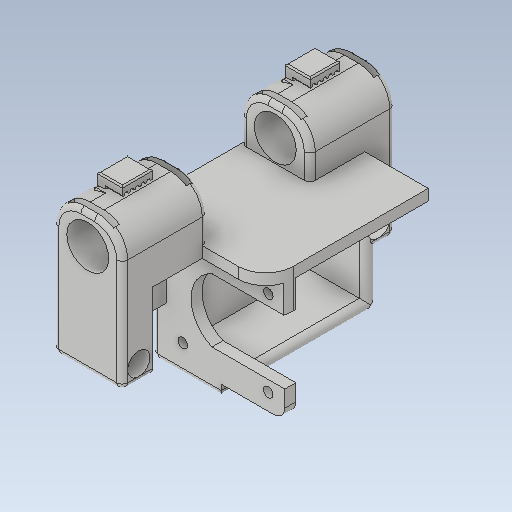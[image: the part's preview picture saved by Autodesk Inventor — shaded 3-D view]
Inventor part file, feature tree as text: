
AUTODESK INVENTOR PART (.ipt)
format: ipt  version: 2020 (Build 240168000, 168)  size: 683,008 bytes
history: native  units: in
note: dims shown in document units (in); Inventor stores cm internally (conversion verified against a paired STEP export)
features: projected_geometry x27, extrude x16, sketch x16, fillet x8, plane x1, pattern_linear x1, mirror x1
ambient origin geometry x8: Origin, YZ Plane, XZ Plane, XY Plane, X Axis, Y Axis, Z Axis, Center Point
bodies: Solid1 (feature_tree)
feature tree (70):
  extrude  "Extrusion1"  Depth=1.2205in
  extrude  "Extrusion2"  Depth=0.748in
  extrude  "Extrusion3"  Depth=0.4921in
  extrude  "Extrusion8"  Depth=0.748in
  fillet  "Fillet1"  Radius=0.2362in
  fillet  "Fillet2"  Radius=1.006in
  extrude  "Extrusion9"  Depth=2.5984in
  plane  "Work Plane2"
  extrude  "Extrusion26"  Depth=0.0787in
  extrude  "Extrusion27"  Depth=0.0827in
  fillet  "Fillet5"  Radius=0.0827in
  pattern_linear  "Rectangular Pattern1"  Count1=2 Spacing1=0.0in
  extrude  "Extrusion28"  Depth=0.1575in TaperAngle=0.0deg
  fillet  "Fillet6"  Radius=0.3937in
  mirror  "Mirror1"
  extrude  "Extrusion20"  Depth=0.3937in
  extrude  "Extrusion21"  Depth=1.6929in
  extrude  "Extrusion22"  Depth=1.6929in
  extrude  "Extrusion23"  Depth=0.1575in
  fillet  "Fillet4"  Radius=0.2362in
  extrude  "Extrusion24"  Depth=0.1575in
  extrude  "Extrusion25"  Depth=0.1575in
  fillet  "Fillet7"  Radius=0.2362in
  extrude  "Extrusion29"  Depth=0.1575in
  extrude  "Extrusion30"  Depth=0.1575in
  fillet  "Fillet8"  Radius=0.1378in
  fillet  "Fillet9"  Radius=0.1378in
  sketch  "Sketch1"  dims[d0=0.9843in d1=0.0in d2=1.2205in]
  sketch  "Sketch3"  dims[d4=0.748in d5=0.0in d6=0.5984in]
  projected_geometry  "Projected Loop1"
  sketch  "Sketch4"  dims[d7=0.4331in d8=0.4921in]
  projected_geometry  "Projected Loop2"
  sketch  "Sketch5"  dims[d9=0.748in d10=0.0in d11=0.3189in d15=0.2362in d19=1.006in]
  projected_geometry  "Projected Loop3"
  projected_geometry  "Projected Loop4"
  projected_geometry  "Projected Loop5"
  sketch  "Sketch9"  dims[d20=1.9488in d21=2.5984in]
  projected_geometry  "Projected Loop9"
  sketch  "Sketch20"  dims[d33=0.3937in d34=0.0787in]
  sketch  "Sketch21"  dims[d43=0.7874in d44=0.0in d45=0.0827in d46=0.0827in]
  projected_geometry  "Projected Loop34"
  sketch  "Sketch22"  dims[d47=0.4764in]
  projected_geometry  "Projected Loop35"
  projected_geometry  "Projected Loop36"
  sketch  "Sketch25"  dims[d49=0.6378in]
  projected_geometry  "Projected Loop47"
  projected_geometry  "Projected Loop48"
  projected_geometry  "Projected Loop49"
  projected_geometry  "Projected Loop50"
  projected_geometry  "Projected Loop51"
  sketch  "Sketch27"  dims[d50=0.6378in]
  projected_geometry  "Projected Loop58"
  projected_geometry  "Projected Loop59"
  projected_geometry  "Projected Loop60"
  sketch  "Sketch28"  dims[d53=0.2402in d54=0.0in]
  projected_geometry  "Projected Loop61"
  sketch  "Sketch29"  dims[d123=0.0394in]
  projected_geometry  "Projected Loop62"
  sketch  "Sketch30"  dims[d125=0.0394in]
  projected_geometry  "Projected Loop63"
  sketch  "Sketch32"  dims[d126=0.1575in d127=0.7874in d128=0.0in]
  projected_geometry  "Projected Loop66"
  projected_geometry  "Projected Loop67"
  projected_geometry  "Projected Loop68"
  sketch  "Sketch33"  dims[d130=0.0in d132=0.1575in d133=0.0in d134=0.3937in]
  projected_geometry  "Projected Loop69"
  projected_geometry  "Projected Loop70"
  projected_geometry  "Projected Loop71"
  sketch  "Sketch34"  dims[d135=1.6929in d136=0.3937in d137=1.6929in d138=1.6929in d140=0.2362in d141=0.2362in d142=0.2362in d143=1.2205in d144=0.2362in d146=1.2205in d147=0.2362in d148=0.1378in d149=0.1378in d150=0.1378in d151=0.1378in d152=0.1181in d153=0.0in d156=1.8898in d158=0.2362in d159=0.2362in d160=0.1181in d161=0.0in d162=0.0787in d164=0.9843in d170=0.8465in d171=0.8465in d172=0.9843in d173=0.1181in d174=0.0in d175=0.1181in d176=0.0in d177=0.4764in d178=0.3543in d179=0.5512in d180=0.0394in d181=0.0in d182=0.1575in d183=0.0in d184=0.0472in d185=0.0335in d186=0.0661in d187=0.0394in d188=0.0394in d191=0.2441in d192=0.0in d193=0.0063in d194=2.7559in d196=0.0787in d197=0.2441in d198=0.0in d199=0.0197in d200=0.3937in d201=0.1575in d202=0.1575in d203=0.0in d204=0.1575in d205=0.0in d206=0.0787in d207=0.1575in]
  projected_geometry  "Projected Loop72"
